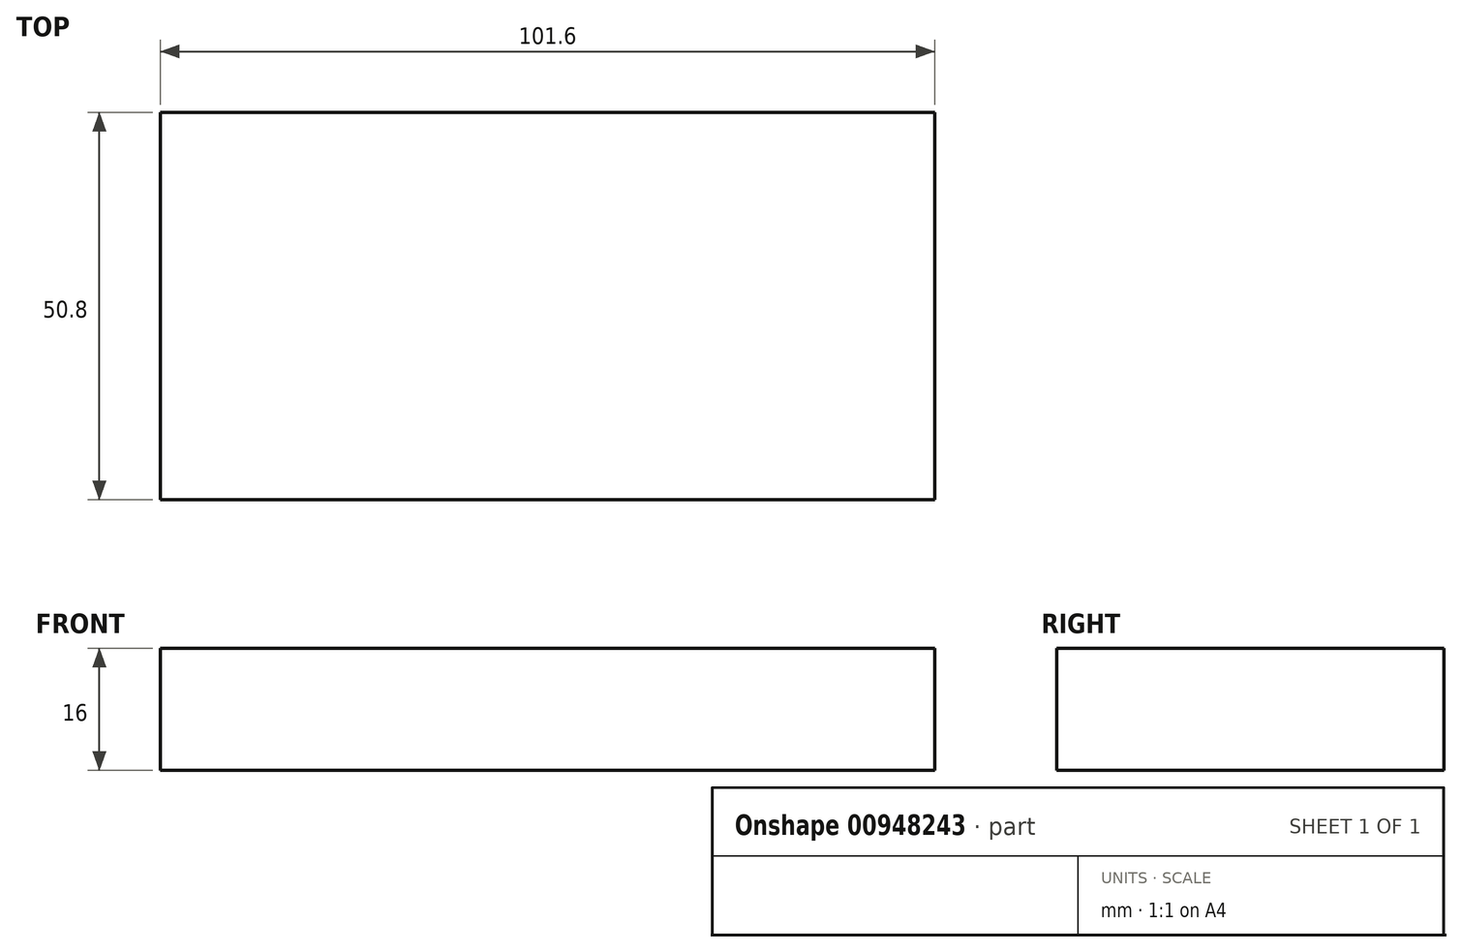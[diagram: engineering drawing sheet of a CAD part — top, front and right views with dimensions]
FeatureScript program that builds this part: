
annotation { "Feature Type Name" : "Feature", "Feature Type Description" : "" }
export const myFeature = defineFeature(function(context is Context, id is Id, definition is map)
    precondition{}
    {
        {
            var Q0;
            Q0=qCreatedBy(makeId("Top.planeOp"),FACE);
            var sketch = newSketch(context, id + "F0", { "sketchPlane" : qUnion([Q0])});
            skLineSegment(sketch, "E0.bottom", {"start": v(0, 0) * mm, "end": v(101.6, 0) * mm});
            skLineSegment(sketch, "E0.top", {"start": v(0, -50.8) * mm, "end": v(101.6, -50.8) * mm});
            skLineSegment(sketch, "E0.left", {"start": v(0, 0) * mm, "end": v(0, -50.8) * mm});
            skLineSegment(sketch, "E0.right", {"start": v(101.6, 0) * mm, "end": v(101.6, -50.8) * mm});
            skSolve(sketch);
        }
        {
            var Q0;
            Q0 = qSketchRegion(id + "F0", true);
            extrude(context, id + "F1", {"entities" : qUnion([Q0]), "depth" : 16 * mm, "offsetDistance" : 25.4 * mm});
        }
    });
